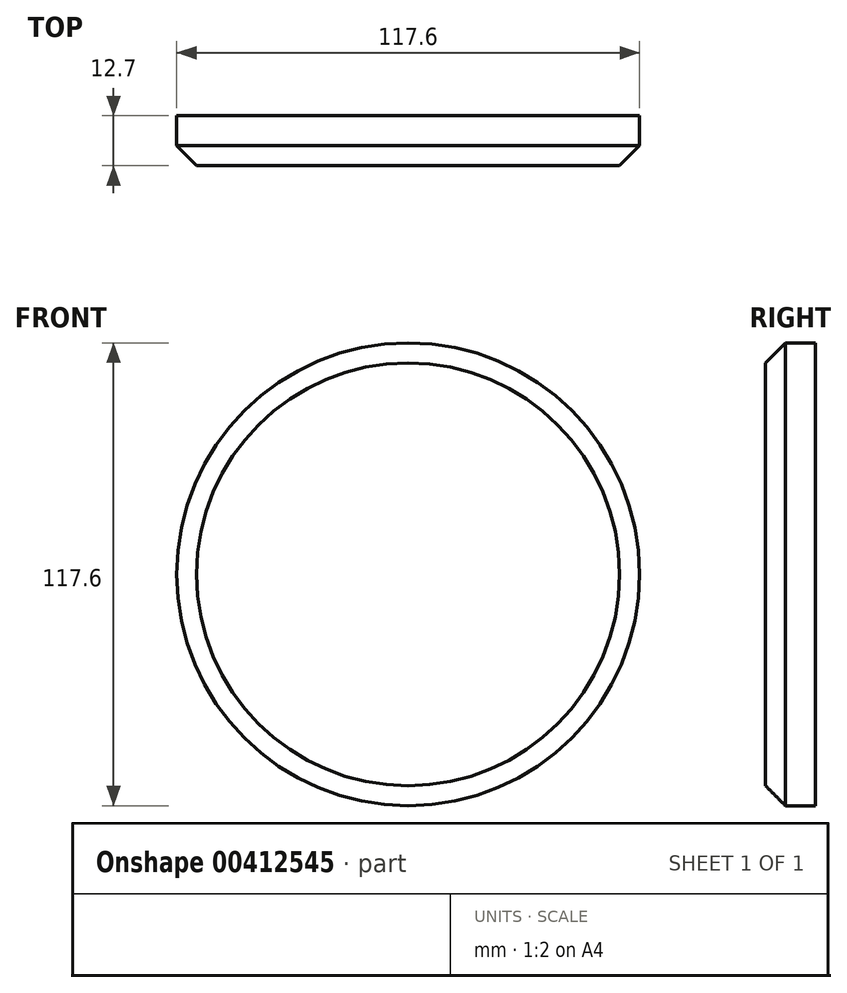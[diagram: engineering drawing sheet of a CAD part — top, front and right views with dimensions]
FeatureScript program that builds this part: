
annotation { "Feature Type Name" : "Feature", "Feature Type Description" : "" }
export const myFeature = defineFeature(function(context is Context, id is Id, definition is map)
    precondition{}
    {
        {
            var Q0;
            Q0=qCreatedBy(makeId("Front.planeOp"),FACE);
            var sketch = newSketch(context, id + "F0", { "sketchPlane" : qUnion([Q0])});
            skCircle(sketch, "E0", {"center": v(0, 0) * mm, "radius": 58.8 * mm});
            skSolve(sketch);
        }
        {
            var Q0;
            Q0=makeQuery(id+"F0.imprint","IMPRINT",FACE,{"disambiguationData":[TD([[makeQuery(id+"F0.imprint","IMPRINT",EDGE,{"derivedFrom":sQuery(id+"F0.wireOp",EDGE,"E0")}),1.0]])]});
            extrude(context, id + "F1", {"entities" : qUnion([Q0]), "depth" : 12.7 * mm, "offsetDistance" : 25.4 * mm});
        }
        {
            var Q0;
            Q0=makeQuery(id+"F1.opExtrude","CAP_FACE",FACE,{"disambiguationData":[OSD([sQuery(id+"F0.wireOp",EDGE,"E0")])],"isStart":false});
            chamfer(context, id + "F2", {"entities" : qUnion([Q0]), "width" : 5.08 * mm, "tangentPropagation" : true});
        }
    });
